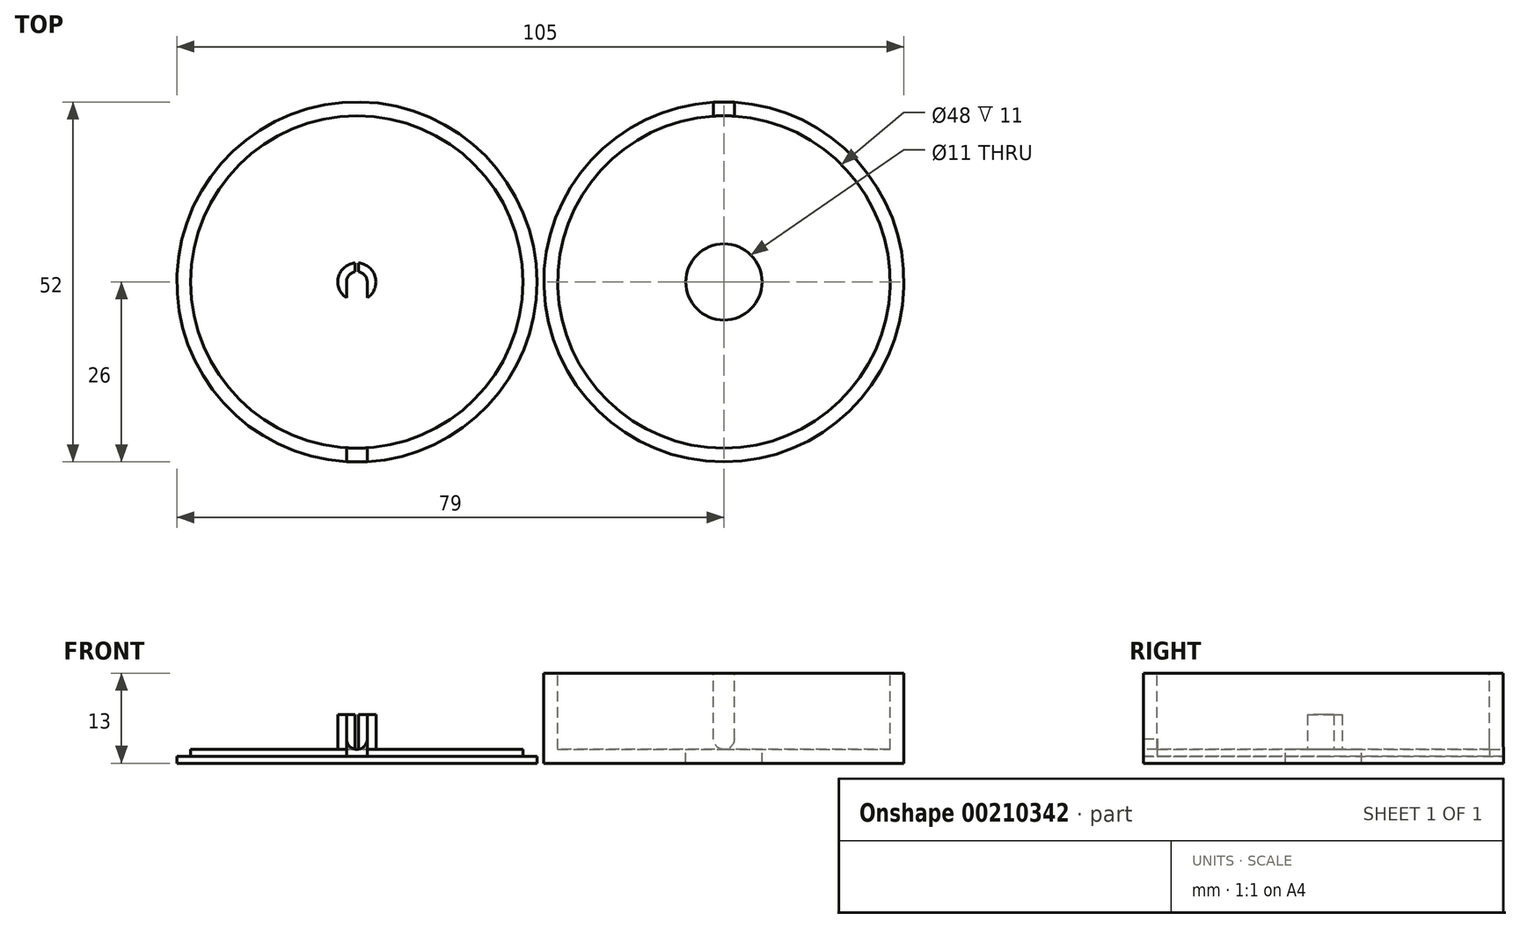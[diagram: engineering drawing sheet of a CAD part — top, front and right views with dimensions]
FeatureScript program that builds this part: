
annotation { "Feature Type Name" : "Feature", "Feature Type Description" : "" }
export const myFeature = defineFeature(function(context is Context, id is Id, definition is map)
    precondition{}
    {
        {
            var Q0;
            Q0=qCreatedBy(makeId("Top.planeOp"),FACE);
            var sketch = newSketch(context, id + "F0", { "sketchPlane" : qUnion([Q0])});
            skCircle(sketch, "E0", {"center": v(0, 0) * mm, "radius": 2.75 * mm});
            skLineSegment(sketch, "E1.bottom", {"start": v(-0.25, -2.75) * mm, "end": v(0.25, -2.75) * mm});
            skLineSegment(sketch, "E1.top", {"start": v(-0.25, 2.75) * mm, "end": v(0.25, 2.75) * mm});
            skLineSegment(sketch, "E1.left", {"start": v(-0.25, -2.75) * mm, "end": v(-0.25, 2.75) * mm});
            skLineSegment(sketch, "E1.right", {"start": v(0.25, -2.75) * mm, "end": v(0.25, 2.75) * mm});
            skCircle(sketch, "E2", {"center": v(0, 0) * mm, "radius": 5.5 * mm});
            skCircle(sketch, "E3", {"center": v(0, 0) * mm, "radius": 26 * mm});
            skCircle(sketch, "E4", {"center": v(0, 0) * mm, "radius": 24 * mm});
            skCircle(sketch, "E5", {"center": v(0, 0) * mm, "radius": 1.5 * mm});
            skSolve(sketch);
        }
        {
            var Q0;
            Q0=makeQuery(id+"F0.imprint","IMPRINT",FACE,{"disambiguationData":[TD([[makeQuery(id+"F0.imprint","IMPRINT",EDGE,{"derivedFrom":sQuery(id+"F0.wireOp",EDGE,"E2")}),1.0]])]});
            var Q1;
            {var subQ0=sQuery(id+"F0.wireOp",EDGE,"E1.top");var subQ1=sQuery(id+"F0.wireOp",EDGE,"E0");var subQ2=makeQuery(id+"F0.imprint","INTERSECT",VERTEX,{"derivedFrom":[subQ1,subQ0]});Q1=makeQuery(id+"F0.imprint","IMPRINT",FACE,{"disambiguationData":[TD([[makeQuery(id+"F0.imprint","IMPRINT",EDGE,{"disambiguationData":[TD([[subQ2,1.0]])],"derivedFrom":subQ1}),-1.0]])]});}
            var Q2;
            {var subQ0=sQuery(id+"F0.wireOp",EDGE,"E1.top");var subQ1=sQuery(id+"F0.wireOp",EDGE,"E0");var subQ2=makeQuery(id+"F0.imprint","INTERSECT",VERTEX,{"derivedFrom":[subQ1,subQ0]});Q2=makeQuery(id+"F0.imprint","IMPRINT",FACE,{"disambiguationData":[TD([[makeQuery(id+"F0.imprint","IMPRINT",EDGE,{"disambiguationData":[TD([[subQ2,-1.0]])],"derivedFrom":subQ1}),-1.0]])]});}
            var Q3;
            {var subQ0=sQuery(id+"F0.wireOp",EDGE,"E1.left");var subQ1=sQuery(id+"F0.wireOp",EDGE,"E0");var subQ2=makeQuery(id+"F0.imprint","INTERSECT",VERTEX,{"disambiguationData":[OD(1.0)],"derivedFrom":[subQ1,subQ0]});Q3=makeQuery(id+"F0.imprint","IMPRINT",FACE,{"disambiguationData":[TD([[makeQuery(id+"F0.imprint","IMPRINT",EDGE,{"disambiguationData":[TD([[subQ2,-1.0]])],"derivedFrom":subQ1}),-1.0]])]});}
            var Q4;
            {var subQ0=sQuery(id+"F0.wireOp",EDGE,"E1.bottom");var subQ1=sQuery(id+"F0.wireOp",EDGE,"E0");var subQ2=makeQuery(id+"F0.imprint","INTERSECT",VERTEX,{"derivedFrom":[subQ1,subQ0]});Q4=makeQuery(id+"F0.imprint","IMPRINT",FACE,{"disambiguationData":[TD([[makeQuery(id+"F0.imprint","IMPRINT",EDGE,{"disambiguationData":[TD([[subQ2,-1.0]])],"derivedFrom":subQ1}),-1.0]])]});}
            var Q5;
            {var subQ0=sQuery(id+"F0.wireOp",EDGE,"E1.left");var subQ1=sQuery(id+"F0.wireOp",EDGE,"E0");var subQ2=makeQuery(id+"F0.imprint","INTERSECT",VERTEX,{"disambiguationData":[OD(0.0)],"derivedFrom":[subQ1,subQ0]});Q5=makeQuery(id+"F0.imprint","IMPRINT",FACE,{"disambiguationData":[TD([[makeQuery(id+"F0.imprint","IMPRINT",EDGE,{"disambiguationData":[TD([[subQ2,-1.0]])],"derivedFrom":subQ1}),1.0]])]});}
            var Q6;
            {var subQ1=sQuery(id+"F0.wireOp",EDGE,"E0");var subQ8=makeQuery(id+"F0.imprint","INTERSECT",VERTEX,{"derivedFrom":[subQ1,sQuery(id+"F0.wireOp",EDGE,"E1.top")]});Q6=makeQuery(id+"F0.imprint","IMPRINT",FACE,{"disambiguationData":[TD([[makeQuery(id+"F0.imprint","IMPRINT",EDGE,{"disambiguationData":[TD([[subQ8,1.0]])],"derivedFrom":subQ1}),1.0]])]});}
            var Q7;
            {var subQ0=sQuery(id+"F0.wireOp",EDGE,"E1.right");var subQ1=sQuery(id+"F0.wireOp",EDGE,"E0");var subQ2=makeQuery(id+"F0.imprint","INTERSECT",VERTEX,{"disambiguationData":[OD(0.0)],"derivedFrom":[subQ1,subQ0]});Q7=makeQuery(id+"F0.imprint","IMPRINT",FACE,{"disambiguationData":[TD([[makeQuery(id+"F0.imprint","IMPRINT",EDGE,{"disambiguationData":[TD([[subQ2,1.0]])],"derivedFrom":subQ1}),1.0]])]});}
            var Q8;
            Q8=makeQuery(id+"F0.imprint","IMPRINT",FACE,{"disambiguationData":[TD([[makeQuery(id+"F0.imprint","IMPRINT",EDGE,{"derivedFrom":sQuery(id+"F0.wireOp",EDGE,"E2")}),-1.0]])]});
            var Q9;
            {var subQ0=sQuery(id+"F0.wireOp",EDGE,"E5");var subQ1=sQuery(id+"F0.wireOp",EDGE,"E1.left");var subQ2=makeQuery(id+"F0.imprint","INTERSECT",VERTEX,{"disambiguationData":[OD(0.0)],"derivedFrom":[subQ1,subQ0]});Q9=makeQuery(id+"F0.imprint","IMPRINT",FACE,{"disambiguationData":[TD([[makeQuery(id+"F0.imprint","IMPRINT",EDGE,{"disambiguationData":[TD([[subQ2,-1.0]])],"derivedFrom":subQ1}),1.0]])]});}
            var Q10;
            {var subQ0=sQuery(id+"F0.wireOp",EDGE,"E5");var subQ1=sQuery(id+"F0.wireOp",EDGE,"E1.right");var subQ2=makeQuery(id+"F0.imprint","INTERSECT",VERTEX,{"disambiguationData":[OD(0.0)],"derivedFrom":[subQ1,subQ0]});Q10=makeQuery(id+"F0.imprint","IMPRINT",FACE,{"disambiguationData":[TD([[makeQuery(id+"F0.imprint","IMPRINT",EDGE,{"disambiguationData":[TD([[subQ2,-1.0]])],"derivedFrom":subQ1}),-1.0]])]});}
            var Q11;
            {var subQ0=sQuery(id+"F0.wireOp",EDGE,"E5");var subQ1=sQuery(id+"F0.wireOp",EDGE,"E1.left");var subQ2=makeQuery(id+"F0.imprint","INTERSECT",VERTEX,{"disambiguationData":[OD(0.0)],"derivedFrom":[subQ1,subQ0]});Q11=makeQuery(id+"F0.imprint","IMPRINT",FACE,{"disambiguationData":[TD([[makeQuery(id+"F0.imprint","IMPRINT",EDGE,{"disambiguationData":[TD([[subQ2,-1.0]])],"derivedFrom":subQ1}),-1.0]])]});}
            var Q12;
            {var subQ0=sQuery(id+"F0.wireOp",EDGE,"E1.left");var subQ1=sQuery(id+"F0.wireOp",EDGE,"E0");var subQ2=makeQuery(id+"F0.imprint","INTERSECT",VERTEX,{"disambiguationData":[OD(1.0)],"derivedFrom":[subQ1,subQ0]});Q12=makeQuery(id+"F0.imprint","IMPRINT",FACE,{"disambiguationData":[TD([[makeQuery(id+"F0.imprint","IMPRINT",EDGE,{"disambiguationData":[TD([[subQ2,-1.0]])],"derivedFrom":subQ1}),1.0]])]});}
            extrude(context, id + "F1", {"entities" : qUnion([Q0, Q1, Q2, Q3, Q4, Q5, Q6, Q7, Q8, Q9, Q10, Q11, Q12]), "depth" : 1 * mm});
        }
        {
            var Q0;
            Q0=makeQuery(id+"F0.imprint","IMPRINT",FACE,{"disambiguationData":[TD([[makeQuery(id+"F0.imprint","IMPRINT",EDGE,{"derivedFrom":sQuery(id+"F0.wireOp",EDGE,"E2")}),1.0]])]});
            var Q1;
            Q1=makeQuery(id+"F0.imprint","IMPRINT",FACE,{"disambiguationData":[TD([[makeQuery(id+"F0.imprint","IMPRINT",EDGE,{"derivedFrom":sQuery(id+"F0.wireOp",EDGE,"E2")}),-1.0]])]});
            var Q2;
            Q2=makeQuery(id+"F0.imprint","IMPRINT",FACE,{"disambiguationData":[TD([[makeQuery(id+"F0.imprint","IMPRINT",EDGE,{"derivedFrom":sQuery(id+"F0.wireOp",EDGE,"E3")}),1.0]])]});
            var Q3;
            {var subQ0=sQuery(id+"F0.wireOp",EDGE,"E1.left");var subQ1=sQuery(id+"F0.wireOp",EDGE,"E0");var subQ2=makeQuery(id+"F0.imprint","INTERSECT",VERTEX,{"disambiguationData":[OD(0.0)],"derivedFrom":[subQ1,subQ0]});Q3=makeQuery(id+"F0.imprint","IMPRINT",FACE,{"disambiguationData":[TD([[makeQuery(id+"F0.imprint","IMPRINT",EDGE,{"disambiguationData":[TD([[subQ2,-1.0]])],"derivedFrom":subQ1}),1.0]])]});}
            var Q4;
            {var subQ0=sQuery(id+"F0.wireOp",EDGE,"E1.right");var subQ1=sQuery(id+"F0.wireOp",EDGE,"E0");var subQ2=makeQuery(id+"F0.imprint","INTERSECT",VERTEX,{"disambiguationData":[OD(0.0)],"derivedFrom":[subQ1,subQ0]});Q4=makeQuery(id+"F0.imprint","IMPRINT",FACE,{"disambiguationData":[TD([[makeQuery(id+"F0.imprint","IMPRINT",EDGE,{"disambiguationData":[TD([[subQ2,1.0]])],"derivedFrom":subQ1}),1.0]])]});}
            var Q5;
            {var subQ1=sQuery(id+"F0.wireOp",EDGE,"E0");var subQ8=makeQuery(id+"F0.imprint","INTERSECT",VERTEX,{"derivedFrom":[subQ1,sQuery(id+"F0.wireOp",EDGE,"E1.top")]});Q5=makeQuery(id+"F0.imprint","IMPRINT",FACE,{"disambiguationData":[TD([[makeQuery(id+"F0.imprint","IMPRINT",EDGE,{"disambiguationData":[TD([[subQ8,1.0]])],"derivedFrom":subQ1}),1.0]])]});}
            var Q6;
            {var subQ0=sQuery(id+"F0.wireOp",EDGE,"E1.left");var subQ1=sQuery(id+"F0.wireOp",EDGE,"E0");var subQ2=makeQuery(id+"F0.imprint","INTERSECT",VERTEX,{"disambiguationData":[OD(1.0)],"derivedFrom":[subQ1,subQ0]});Q6=makeQuery(id+"F0.imprint","IMPRINT",FACE,{"disambiguationData":[TD([[makeQuery(id+"F0.imprint","IMPRINT",EDGE,{"disambiguationData":[TD([[subQ2,-1.0]])],"derivedFrom":subQ1}),-1.0]])]});}
            var Q7;
            {var subQ0=sQuery(id+"F0.wireOp",EDGE,"E1.top");var subQ1=sQuery(id+"F0.wireOp",EDGE,"E0");var subQ2=makeQuery(id+"F0.imprint","INTERSECT",VERTEX,{"derivedFrom":[subQ1,subQ0]});Q7=makeQuery(id+"F0.imprint","IMPRINT",FACE,{"disambiguationData":[TD([[makeQuery(id+"F0.imprint","IMPRINT",EDGE,{"disambiguationData":[TD([[subQ2,1.0]])],"derivedFrom":subQ1}),-1.0]])]});}
            var Q8;
            {var subQ0=sQuery(id+"F0.wireOp",EDGE,"E1.bottom");var subQ1=sQuery(id+"F0.wireOp",EDGE,"E0");var subQ2=makeQuery(id+"F0.imprint","INTERSECT",VERTEX,{"derivedFrom":[subQ1,subQ0]});Q8=makeQuery(id+"F0.imprint","IMPRINT",FACE,{"disambiguationData":[TD([[makeQuery(id+"F0.imprint","IMPRINT",EDGE,{"disambiguationData":[TD([[subQ2,-1.0]])],"derivedFrom":subQ1}),-1.0]])]});}
            var Q9;
            {var subQ0=sQuery(id+"F0.wireOp",EDGE,"E1.top");var subQ1=sQuery(id+"F0.wireOp",EDGE,"E0");var subQ2=makeQuery(id+"F0.imprint","INTERSECT",VERTEX,{"derivedFrom":[subQ1,subQ0]});Q9=makeQuery(id+"F0.imprint","IMPRINT",FACE,{"disambiguationData":[TD([[makeQuery(id+"F0.imprint","IMPRINT",EDGE,{"disambiguationData":[TD([[subQ2,-1.0]])],"derivedFrom":subQ1}),-1.0]])]});}
            var Q10;
            Q10=makeQuery(id+"F1.opExtrude","CAP_FACE",FACE,{"disambiguationData":[OSD([sQuery(id+"F0.wireOp",EDGE,"E4")])],"isStart":false});
            var Q11;
            Q11=makeQuery(id+"F1.opExtrude","CAP_FACE",FACE,{"disambiguationData":[OSD([sQuery(id+"F0.wireOp",EDGE,"E4")])],"isStart":true});
            var Q12;
            {var subQ0=sQuery(id+"F0.wireOp",EDGE,"E5");var subQ1=sQuery(id+"F0.wireOp",EDGE,"E1.left");var subQ2=makeQuery(id+"F0.imprint","INTERSECT",VERTEX,{"disambiguationData":[OD(0.0)],"derivedFrom":[subQ1,subQ0]});Q12=makeQuery(id+"F0.imprint","IMPRINT",FACE,{"disambiguationData":[TD([[makeQuery(id+"F0.imprint","IMPRINT",EDGE,{"disambiguationData":[TD([[subQ2,-1.0]])],"derivedFrom":subQ1}),1.0]])]});}
            var Q13;
            {var subQ0=sQuery(id+"F0.wireOp",EDGE,"E5");var subQ1=sQuery(id+"F0.wireOp",EDGE,"E1.right");var subQ2=makeQuery(id+"F0.imprint","INTERSECT",VERTEX,{"disambiguationData":[OD(0.0)],"derivedFrom":[subQ1,subQ0]});Q13=makeQuery(id+"F0.imprint","IMPRINT",FACE,{"disambiguationData":[TD([[makeQuery(id+"F0.imprint","IMPRINT",EDGE,{"disambiguationData":[TD([[subQ2,-1.0]])],"derivedFrom":subQ1}),-1.0]])]});}
            var Q14;
            {var subQ0=sQuery(id+"F0.wireOp",EDGE,"E5");var subQ1=sQuery(id+"F0.wireOp",EDGE,"E1.left");var subQ2=makeQuery(id+"F0.imprint","INTERSECT",VERTEX,{"disambiguationData":[OD(0.0)],"derivedFrom":[subQ1,subQ0]});Q14=makeQuery(id+"F0.imprint","IMPRINT",FACE,{"disambiguationData":[TD([[makeQuery(id+"F0.imprint","IMPRINT",EDGE,{"disambiguationData":[TD([[subQ2,-1.0]])],"derivedFrom":subQ1}),-1.0]])]});}
            var Q15;
            {var subQ0=sQuery(id+"F0.wireOp",EDGE,"E1.left");var subQ1=sQuery(id+"F0.wireOp",EDGE,"E0");var subQ2=makeQuery(id+"F0.imprint","INTERSECT",VERTEX,{"disambiguationData":[OD(1.0)],"derivedFrom":[subQ1,subQ0]});Q15=makeQuery(id+"F0.imprint","IMPRINT",FACE,{"disambiguationData":[TD([[makeQuery(id+"F0.imprint","IMPRINT",EDGE,{"disambiguationData":[TD([[subQ2,-1.0]])],"derivedFrom":subQ1}),1.0]])]});}
            extrude(context, id + "F2", {"entities" : qUnion([Q0, Q1, Q2, Q3, Q4, Q5, Q6, Q7, Q8, Q9, Q10, Q11, Q12, Q13, Q14, Q15]), "operationType" : NewBodyOperationType.ADD, "oppositeDirection" : true, "depth" : 1 * mm});
        }
        {
            var Q0;
            {var subQ0=sQuery(id+"F0.wireOp",EDGE,"E1.left");var subQ1=sQuery(id+"F0.wireOp",EDGE,"E0");var subQ2=makeQuery(id+"F0.imprint","INTERSECT",VERTEX,{"disambiguationData":[OD(0.0)],"derivedFrom":[subQ1,subQ0]});Q0=makeQuery(id+"F0.imprint","IMPRINT",FACE,{"disambiguationData":[TD([[makeQuery(id+"F0.imprint","IMPRINT",EDGE,{"disambiguationData":[TD([[subQ2,-1.0]])],"derivedFrom":subQ1}),1.0]])]});}
            var Q1;
            {var subQ0=sQuery(id+"F0.wireOp",EDGE,"E1.right");var subQ1=sQuery(id+"F0.wireOp",EDGE,"E0");var subQ2=makeQuery(id+"F0.imprint","INTERSECT",VERTEX,{"disambiguationData":[OD(0.0)],"derivedFrom":[subQ1,subQ0]});Q1=makeQuery(id+"F0.imprint","IMPRINT",FACE,{"disambiguationData":[TD([[makeQuery(id+"F0.imprint","IMPRINT",EDGE,{"disambiguationData":[TD([[subQ2,1.0]])],"derivedFrom":subQ1}),1.0]])]});}
            extrude(context, id + "F3", {"entities" : qUnion([Q0, Q1]), "operationType" : NewBodyOperationType.ADD, "depth" : 6 * mm});
        }
        {
            var Q0;
            Q0=makeQuery(id+"F0.imprint","IMPRINT",FACE,{"disambiguationData":[TD([[makeQuery(id+"F0.imprint","IMPRINT",EDGE,{"derivedFrom":sQuery(id+"F0.wireOp",EDGE,"E3")}),1.0]])]});
            extrude(context, id + "F4", {"entities" : qUnion([Q0]), "depth" : 13 * mm});
        }
        {
            var Q0;
            Q0=makeQuery(id+"F0.imprint","IMPRINT",FACE,{"disambiguationData":[TD([[makeQuery(id+"F0.imprint","IMPRINT",EDGE,{"derivedFrom":sQuery(id+"F0.wireOp",EDGE,"E2")}),-1.0]])]});
            extrude(context, id + "F5", {"entities" : qUnion([Q0]), "operationType" : NewBodyOperationType.ADD, "depth" : 13 * mm, "hasSecondDirection" : true, "secondDirectionOppositeDirection" : false, "secondDirectionDepth" : 11 * mm});
        }
        {
            var Q0;
            Q0=qCreatedBy(makeId("Front.planeOp"),FACE);
            var sketch = newSketch(context, id + "F6", { "sketchPlane" : qUnion([Q0])});
            skLineSegment(sketch, "E6.bottom", {"start": v(1.5, 1) * mm, "end": v(-1.5, 1) * mm});
            skLineSegment(sketch, "E6.top", {"start": v(1.5, 11) * mm, "end": v(-1.5, 11) * mm});
            skLineSegment(sketch, "E6.left", {"start": v(1.5, 1) * mm, "end": v(1.5, 11) * mm});
            skLineSegment(sketch, "E6.right", {"start": v(-1.5, 1) * mm, "end": v(-1.5, 11) * mm});
            skPoint(sketch, "E6.middle", {"position": v(0, 6) * mm});
            skLineSegment(sketch, "E7.bottom", {"start": v(1.5, 0) * mm, "end": v(-1.5, 0) * mm});
            skLineSegment(sketch, "E7.top", {"start": v(1.5, 4) * mm, "end": v(-1.5, 4) * mm});
            skLineSegment(sketch, "E7.left", {"start": v(1.5, 0) * mm, "end": v(1.5, 4) * mm});
            skLineSegment(sketch, "E7.right", {"start": v(-1.5, 0) * mm, "end": v(-1.5, 4) * mm});
            skPoint(sketch, "E7.middle", {"position": v(0, 2) * mm});
            skSolve(sketch);
        }
        {
            var Q0;
            Q0=makeQuery(id+"F6.imprint","IMPRINT",FACE,{"disambiguationData":[TD([[makeQuery(id+"F6.imprint","IMPRINT",EDGE,{"derivedFrom":sQuery(id+"F6.wireOp",EDGE,"E6.top")}),1.0]])]});
            var Q1;
            {var subQ0=sQuery(id+"F6.wireOp",EDGE,"E6.bottom");Q1=makeQuery(id+"F6.imprint","IMPRINT",FACE,{"disambiguationData":[TD([[makeQuery(id+"F6.imprint","IMPRINT",EDGE,{"derivedFrom":subQ0}),-1.0]])]});}
            extrude(context, id + "F7", {"entities" : qUnion([Q0, Q1]), "operationType" : NewBodyOperationType.REMOVE, "depth" : 30 * mm});
        }
        {
            var Q0;
            Q0=makeQuery(id+"F7.boolean.opBoolean","COPY",EDGE,{"derivedFrom":makeQuery(id+"F7.opExtrude","SWEPT_EDGE",EDGE,{"disambiguationData":[OSD([sQuery(id+"F6.wireOp",EDGE,"E6.top"),sQuery(id+"F6.wireOp",EDGE,"E6.right")])]})});
            var Q1;
            Q1=makeQuery(id+"F7.boolean.opBoolean","COPY",EDGE,{"derivedFrom":makeQuery(id+"F7.opExtrude","SWEPT_EDGE",EDGE,{"disambiguationData":[OSD([sQuery(id+"F6.wireOp",EDGE,"E6.top"),sQuery(id+"F6.wireOp",EDGE,"E6.left")])]})});
            var Q2;
            Q2=makeQuery(id+"F7.boolean.opBoolean","COPY",EDGE,{"derivedFrom":makeQuery(id+"F7.opExtrude","SWEPT_EDGE",EDGE,{"disambiguationData":[OSD([sQuery(id+"F6.wireOp",EDGE,"E6.bottom"),sQuery(id+"F6.wireOp",EDGE,"E7.right")])]})});
            var Q3;
            Q3=makeQuery(id+"F7.boolean.opBoolean","COPY",EDGE,{"derivedFrom":makeQuery(id+"F7.opExtrude","SWEPT_EDGE",EDGE,{"disambiguationData":[OSD([sQuery(id+"F6.wireOp",EDGE,"E6.bottom"),sQuery(id+"F6.wireOp",EDGE,"E7.left")])]})});
            fillet(context, id + "F8", {"entities" : qUnion([Q0, Q1, Q2, Q3]), "radius" : 1.5 * mm, "tangentPropagation" : true, "allowEdgeOverflow" : false});
        }
        {
            var Q0;
            {var subQ0=sQuery(id+"F6.wireOp",EDGE,"E6.bottom");Q0=makeQuery(id+"F6.imprint","IMPRINT",FACE,{"disambiguationData":[TD([[makeQuery(id+"F6.imprint","IMPRINT",EDGE,{"derivedFrom":subQ0}),-1.0]])]});}
            var Q1;
            {var subQ0=sQuery(id+"F6.wireOp",EDGE,"E6.bottom");Q1=makeQuery(id+"F6.imprint","IMPRINT",FACE,{"disambiguationData":[TD([[makeQuery(id+"F6.imprint","IMPRINT",EDGE,{"derivedFrom":subQ0}),1.0]])]});}
            extrude(context, id + "F9", {"entities" : qUnion([Q0, Q1]), "depth" : 30 * mm});
        }
        {
            var Q0;
            Q0=makeQuery(id+"F4.opExtrude","SWEPT_BODY",BODY,{"disambiguationData":[OSD([sQuery(id+"F0.wireOp",EDGE,"E3"),sQuery(id+"F0.wireOp",EDGE,"E4")])]});
            var Q1;
            Q1=makeQuery(id+"F9.opExtrude","SWEPT_BODY",BODY,{"disambiguationData":[OSD([sQuery(id+"F6.wireOp",EDGE,"E7.bottom"),sQuery(id+"F6.wireOp",EDGE,"E7.top"),sQuery(id+"F6.wireOp",EDGE,"E7.left"),sQuery(id+"F6.wireOp",EDGE,"E7.right")])]});
            booleanBodies(context, id + "F10", {"operationType" : BooleanOperationType.INTERSECTION, "tools" : qUnion([Q0, Q1]), "keepTools" : true});
        }
        {
            var Q0;
            Q0=makeQuery(id+"F9.opExtrude","SWEPT_BODY",BODY,{"disambiguationData":[OSD([sQuery(id+"F6.wireOp",EDGE,"E7.bottom"),sQuery(id+"F6.wireOp",EDGE,"E7.top"),sQuery(id+"F6.wireOp",EDGE,"E7.left"),sQuery(id+"F6.wireOp",EDGE,"E7.right")])]});
            var Q1;
            Q1=makeQuery(id+"F4.opExtrude","SWEPT_BODY",BODY,{"disambiguationData":[OSD([sQuery(id+"F0.wireOp",EDGE,"E3"),sQuery(id+"F0.wireOp",EDGE,"E4")])]});
            booleanBodies(context, id + "F11", {"operationType" : BooleanOperationType.SUBTRACTION, "tools" : qUnion([Q0]), "targets" : qUnion([Q1])});
        }
        {
            var Q0;
            Q0=qCreatedBy(makeId("Front.planeOp"),FACE);
            var sketch = newSketch(context, id + "F12", { "sketchPlane" : qUnion([Q0])});
            skLineSegment(sketch, "E8", {"start": v(-36.72, 6) * mm, "end": v(41.59, 6) * mm, "construction": true});
            skSolve(sketch);
        }
        {
            var Q0;
            Q0=makeQuery(id+"F4.opExtrude","SWEPT_BODY",BODY,{"disambiguationData":[OSD([sQuery(id+"F0.wireOp",EDGE,"E3"),sQuery(id+"F0.wireOp",EDGE,"E4")])]});
            var Q1;
            Q1=sQuery(id+"F12.wireOp",EDGE,"E8");
            transform(context, id + "F13", {"entities" : qUnion([Q0]), "transformType" : TransformType.ROTATION, "transformAxis" : qUnion([Q1]), "angle" : 180 * degree, "makeCopy" : false});
        }
        {
            var Q0;
            Q0=makeQuery(id+"F4.opExtrude","SWEPT_BODY",BODY,{"disambiguationData":[OSD([sQuery(id+"F0.wireOp",EDGE,"E3"),sQuery(id+"F0.wireOp",EDGE,"E4")])]});
            transform(context, id + "F14", {"entities" : qUnion([Q0]), "transformType" : TransformType.TRANSLATION_3D, "dx" : 53 * mm, "dy" : 0 * mm, "dz" : 0 * mm, "makeCopy" : false});
        }
    });
